# Revit family: Shower-Bath_Screen-KOHLER-Aerie-K-707205_1
name_source: partatom
category: Specialty Equipment
units: mm (PartAtom-declared; Revit-internal decimal feet)

## family parameters
Cut with Voids When Loaded = No
Host = Face
OmniClass Number = 23.31.17.17
OmniClass Title = Shower Enclosures
Part Type = Normal
Room Calculation Point = No
Round Connector Dimension = Use Diameter
Shared = No

## types (1)
- SHP-Bright Polished Silver
    ADA Compliant = No
    Assembly Code = C1030200
    Date Modified = 07/13/2023
    Default Elevation = 4"
    Description = 32 Inch Bath Screen
    Finish = Kohler-Metal-SHP-Bright_Polished_Silver
    Hardware Included = No
    Height = 57 1/16"
    Length = 1 1/4"
    Manufacturer = Kohler Co.
    Master Format 2014 = 10 28 19.16
    Master Format 2014 Name = Shower Doors
    Material = Premium Metal Construction
    Model = K-707205-L-SHP
    Product Documentation Link = https://www.us.kohler.com
    Product Name = Aerie
    Product Page URL = http://www.us.kohler.com
    Type = 1
    URL = https://www.us.kohler.com
    WaterSense Certified = No

## geometry (parser evidence)
native form markers: Sweep x4
no freeform markers — native parametric forms only
